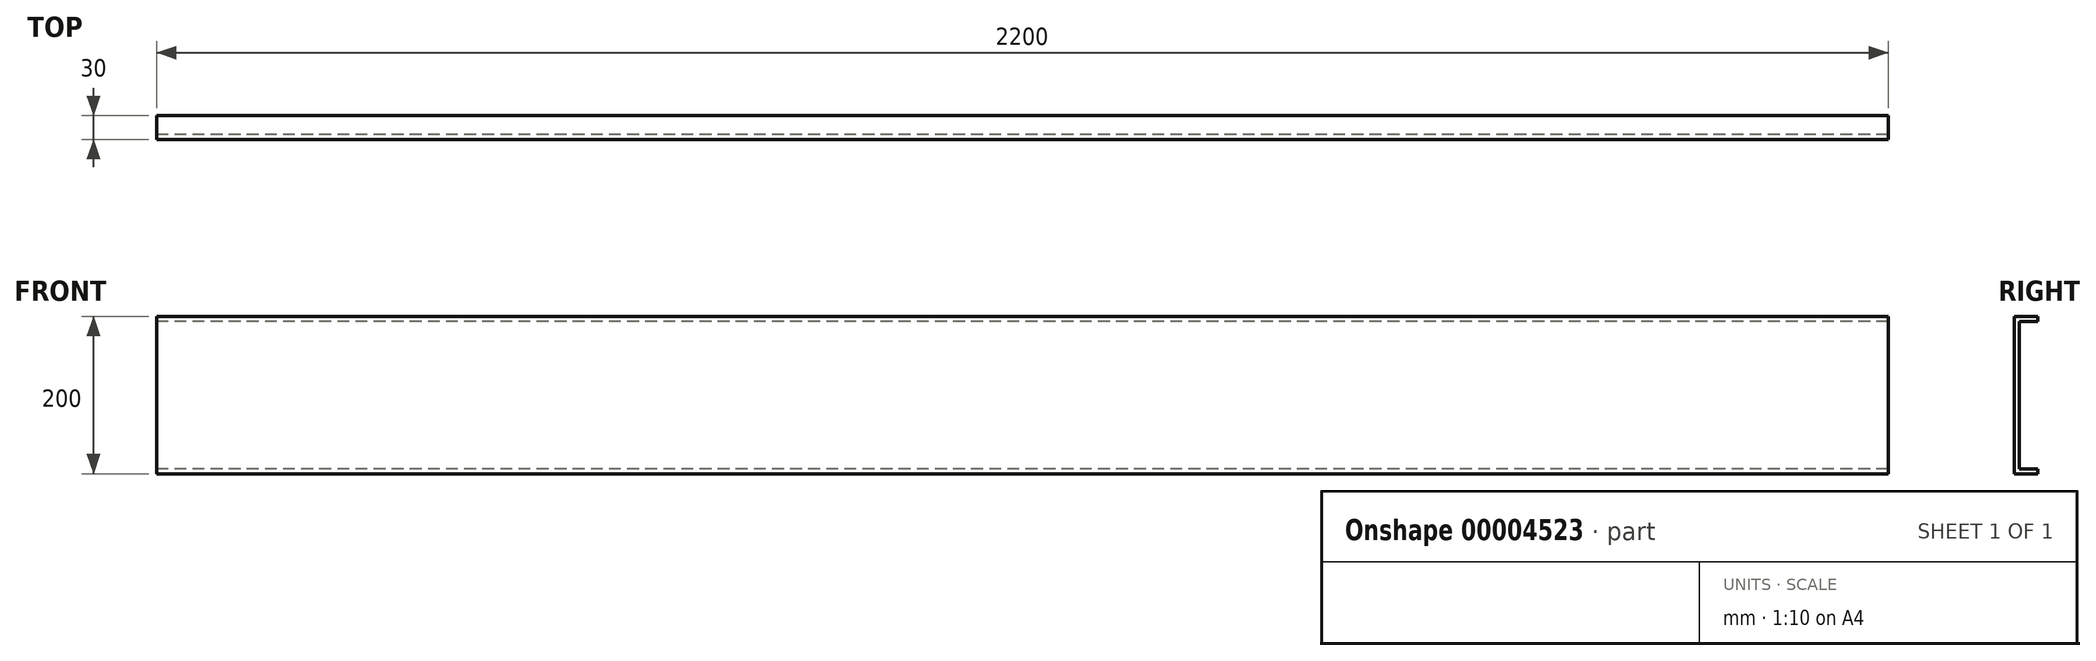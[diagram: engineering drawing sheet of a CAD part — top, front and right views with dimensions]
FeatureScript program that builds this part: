
annotation { "Feature Type Name" : "Feature", "Feature Type Description" : "" }
export const myFeature = defineFeature(function(context is Context, id is Id, definition is map)
    precondition{}
    {
        {
            var Q0;
            Q0=qCreatedBy(makeId("Right.planeOp"),FACE);
            var sketch = newSketch(context, id + "F0", { "sketchPlane" : qUnion([Q0])});
            skLineSegment(sketch, "E0", {"start": v(0, 0) * mm, "end": v(0, 93.65) * mm});
            skLineSegment(sketch, "E1", {"start": v(0, 93.65) * mm, "end": v(23.65, 93.65) * mm});
            skLineSegment(sketch, "E2.0", {"start": v(-6.35, 100) * mm, "end": v(23.65, 100) * mm});
            skLineSegment(sketch, "E2.1", {"start": v(-6.35, 0) * mm, "end": v(-6.35, 100) * mm});
            skLineSegment(sketch, "E3", {"start": v(23.65, 100) * mm, "end": v(23.65, 93.65) * mm});
            skLineSegment(sketch, "E4", {"start": v(0, 0) * mm, "end": v(-6.35, 0) * mm, "construction": true});
            skLineSegment(sketch, "E5.0.MirrorCS", {"start": v(-6.35, 0) * mm, "end": v(-6.35, -100) * mm});
            skLineSegment(sketch, "E6.0.MirrorCS", {"start": v(-6.35, -100) * mm, "end": v(23.65, -100) * mm});
            skLineSegment(sketch, "E7.0.MirrorCS", {"start": v(23.65, -100) * mm, "end": v(23.65, -93.65) * mm});
            skLineSegment(sketch, "E8.0.MirrorCS", {"start": v(0, -93.65) * mm, "end": v(23.65, -93.65) * mm});
            skLineSegment(sketch, "E9.0.MirrorCS", {"start": v(0, 0) * mm, "end": v(0, -93.65) * mm});
            skSolve(sketch);
        }
        {
            var Q0;
            Q0=makeQuery(id+"F0.imprint","IMPRINT",FACE,{"disambiguationData":[TD([[makeQuery(id+"F0.imprint","IMPRINT",EDGE,{"derivedFrom":sQuery(id+"F0.wireOp",EDGE,"E1")}),1.0]])]});
            extrude(context, id + "F1", {"entities" : qUnion([Q0]), "endBound" : BoundingType.SYMMETRIC, "depth" : 2200 * mm});
        }
    });
